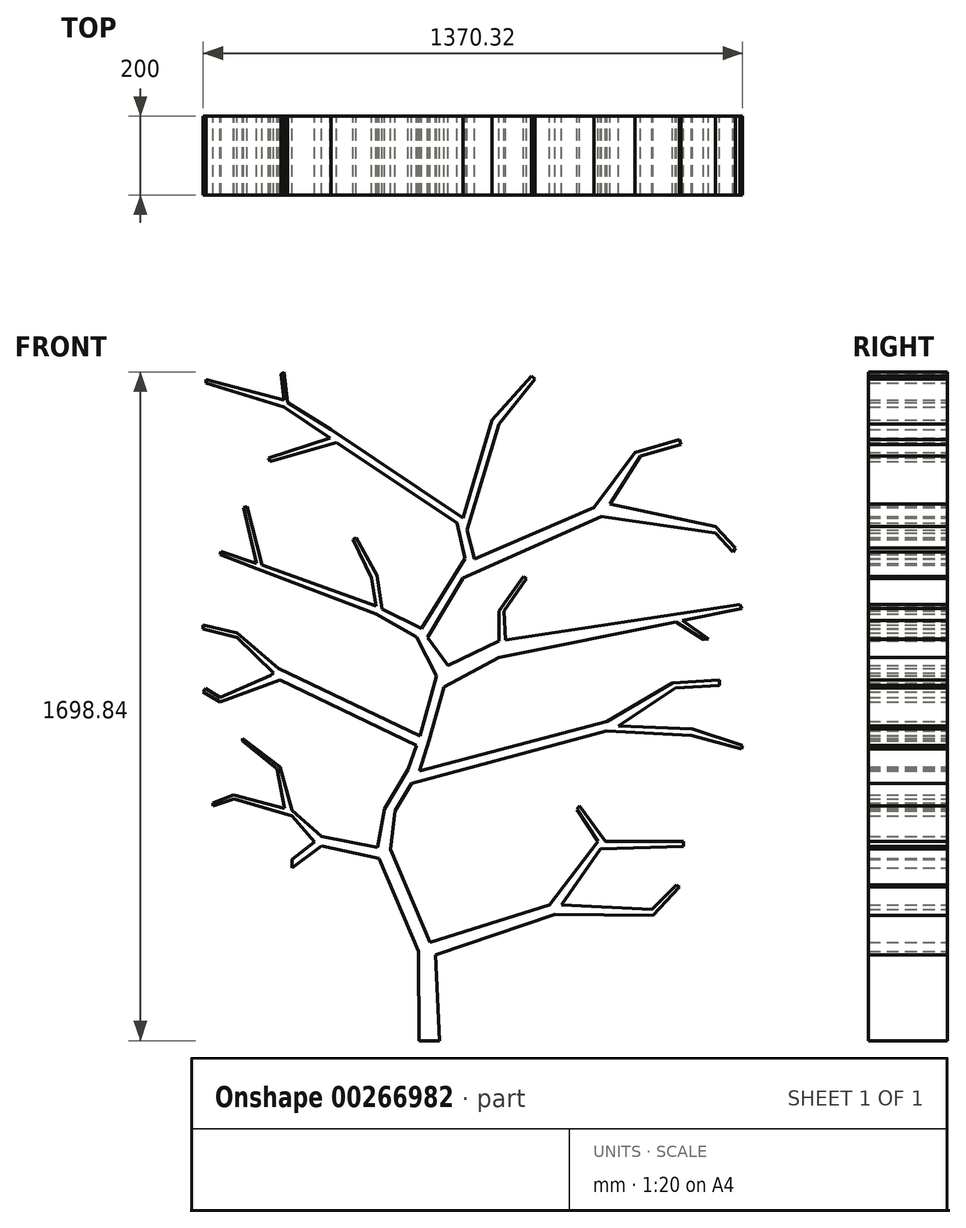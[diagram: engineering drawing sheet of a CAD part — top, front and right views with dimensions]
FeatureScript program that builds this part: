
annotation { "Feature Type Name" : "Feature", "Feature Type Description" : "" }
export const myFeature = defineFeature(function(context is Context, id is Id, definition is map)
    precondition{}
    {
        {
            var Q0;
            Q0=qCreatedBy(makeId("Front.planeOp"),FACE);
            var sketch = newSketch(context, id + "F0", { "sketchPlane" : qUnion([Q0])});
            skLineSegment(sketch, "E0", {"start": v(0, 0) * mm, "end": v(0, 750) * mm, "construction": true});
            skLineSegment(sketch, "E1", {"start": v(0, 750) * mm, "end": v(0, 0) * mm, "construction": true});
            skLineSegment(sketch, "E2", {"start": v(0, 0) * mm, "end": v(0, -750) * mm, "construction": true});
            skLineSegment(sketch, "E3", {"start": v(0, -750) * mm, "end": v(26, -750) * mm});
            skLineSegment(sketch, "E4", {"start": v(0, -750) * mm, "end": v(-26, -750) * mm});
            skLineSegment(sketch, "E5", {"start": v(0, -750) * mm, "end": v(0, -500) * mm, "construction": true});
            skLineSegment(sketch, "E6", {"start": v(-27.5, -522.62) * mm, "end": v(-26, -750) * mm});
            skLineSegment(sketch, "E7", {"start": v(-27.5, -522.62) * mm, "end": v(16.36, -532.36) * mm});
            skLineSegment(sketch, "E8", {"start": v(16.36, -532.36) * mm, "end": v(26, -750) * mm});
            skLineSegment(sketch, "E9", {"start": v(-86.68, -166.63) * mm, "end": v(-114.15, -161.22) * mm});
            skLineSegment(sketch, "E10", {"start": v(-98.77, -264.27) * mm, "end": v(16.36, -532.36) * mm});
            skLineSegment(sketch, "E11", {"start": v(-114.15, -161.22) * mm, "end": v(-131.21, -258.61) * mm});
            skLineSegment(sketch, "E12", {"start": v(-98.77, -264.27) * mm, "end": v(-86.68, -166.63) * mm});
            skLineSegment(sketch, "E13", {"start": v(-27.5, -522.62) * mm, "end": v(-137.38, -264.27) * mm});
            skPoint(sketch, "E14.endSnap0", {"position": v(-273.43, -243.18) * mm});
            skLineSegment(sketch, "E15", {"start": v(-348.87, -310.64) * mm, "end": v(-273.43, -255.18) * mm});
            skLineSegment(sketch, "E16", {"start": v(-348.87, -310.64) * mm, "end": v(-518.95, -310.64) * mm});
            skLineSegment(sketch, "E17", {"start": v(-518.95, -310.64) * mm, "end": v(-518.95, -300.64) * mm});
            skLineSegment(sketch, "E18", {"start": v(-518.95, -300.64) * mm, "end": v(-348.87, -289.78) * mm});
            skLineSegment(sketch, "E19", {"start": v(-273.43, -231.18) * mm, "end": v(-348.87, -164.52) * mm});
            skLineSegment(sketch, "E20", {"start": v(-348.87, -179.1) * mm, "end": v(-496.07, -135.48) * mm});
            skLineSegment(sketch, "E21", {"start": v(-496.07, -135.48) * mm, "end": v(-496.71, -125.5) * mm});
            skLineSegment(sketch, "E22", {"start": v(-496.71, -125.5) * mm, "end": v(-348.87, -164.52) * mm});
            skPoint(sketch, "E23.endSnap0", {"position": v(-422.79, -145.01) * mm});
            skLineSegment(sketch, "E24", {"start": v(-496.07, -135.48) * mm, "end": v(-548.63, -153.46) * mm});
            skLineSegment(sketch, "E25", {"start": v(-496.71, -125.5) * mm, "end": v(-548.63, -146.18) * mm});
            skLineSegment(sketch, "E26", {"start": v(-548.63, -146.18) * mm, "end": v(-548.63, -153.46) * mm});
            skLineSegment(sketch, "E27", {"start": v(-386.86, -60.16) * mm, "end": v(-367.22, -159.68) * mm});
            skLineSegment(sketch, "E28", {"start": v(-474.73, 18.31) * mm, "end": v(-474.73, 11.25) * mm});
            skLineSegment(sketch, "E29", {"start": v(-474.73, 11.25) * mm, "end": v(-386.86, -60.16) * mm});
            skLineSegment(sketch, "E30", {"start": v(-348.87, -179.1) * mm, "end": v(-348.87, -164.52) * mm});
            skLineSegment(sketch, "E31", {"start": v(-273.43, -231.18) * mm, "end": v(-131.21, -258.61) * mm});
            skLineSegment(sketch, "E32", {"start": v(-86.68, -166.63) * mm, "end": v(-24.85, -64.5) * mm});
            skLineSegment(sketch, "E33", {"start": v(-114.15, -161.22) * mm, "end": v(-53.7, -61.36) * mm});
            skLineSegment(sketch, "E34", {"start": v(-379.17, 166.4) * mm, "end": v(-531.36, 110.48) * mm});
            skLineSegment(sketch, "E35", {"start": v(-531.36, 110.48) * mm, "end": v(-551.07, 122.41) * mm});
            skLineSegment(sketch, "E36", {"start": v(-551.07, 122.41) * mm, "end": v(-573.98, 136.29) * mm});
            skLineSegment(sketch, "E37", {"start": v(-573.98, 136.29) * mm, "end": v(-568.07, 144.35) * mm});
            skLineSegment(sketch, "E38", {"start": v(-568.07, 144.35) * mm, "end": v(-531.83, 122.41) * mm});
            skLineSegment(sketch, "E39", {"start": v(-573.98, 295.89) * mm, "end": v(-573.98, 305.89) * mm});
            skLineSegment(sketch, "E40", {"start": v(-498.86, 342.03) * mm, "end": v(-507.68, 340.22) * mm});
            skLineSegment(sketch, "E41", {"start": v(-507.68, 340.22) * mm, "end": v(-498.86, 288.04) * mm});
            skLineSegment(sketch, "E42", {"start": v(-382.8, 195.37) * mm, "end": v(0, 13.26) * mm});
            skLineSegment(sketch, "E43", {"start": v(-488.64, 274.76) * mm, "end": v(-488.3, 285.3) * mm});
            skLineSegment(sketch, "E44", {"start": v(-488.64, 274.76) * mm, "end": v(-573.98, 295.89) * mm});
            skLineSegment(sketch, "E45", {"start": v(-498.86, 342.03) * mm, "end": v(-488.3, 285.3) * mm});
            skLineSegment(sketch, "E46", {"start": v(0, 13.26) * mm, "end": v(-24.85, -64.5) * mm});
            skLineSegment(sketch, "E47", {"start": v(-474.73, 18.31) * mm, "end": v(-379.07, -54.81) * mm});
            skLineSegment(sketch, "E48", {"start": v(-379.07, -54.81) * mm, "end": v(-348.87, -164.52) * mm});
            skLineSegment(sketch, "E49", {"start": v(-24.85, -64.5) * mm, "end": v(-53.7, -61.36) * mm});
            skLineSegment(sketch, "E50", {"start": v(18.3, 176.27) * mm, "end": v(-32.87, 275.32) * mm});
            skPoint(sketch, "E51.endSnap0", {"position": v(-435.55, 240.34) * mm});
            skLineSegment(sketch, "E52", {"start": v(-435.55, 448.7) * mm, "end": v(-531.1, 485.46) * mm});
            skLineSegment(sketch, "E53.1", {"start": v(47.7, 203.3) * mm, "end": v(-19.99, 296.75) * mm});
            skLineSegment(sketch, "E54", {"start": v(-463.33, 606.58) * mm, "end": v(-424.82, 458.12) * mm});
            skLineSegment(sketch, "E55", {"start": v(-531.1, 485.46) * mm, "end": v(-528.35, 492.64) * mm});
            skLineSegment(sketch, "E56", {"start": v(-528.35, 492.64) * mm, "end": v(-424.82, 458.12) * mm});
            skLineSegment(sketch, "E57", {"start": v(-435.55, 448.7) * mm, "end": v(-424.82, 458.12) * mm});
            skLineSegment(sketch, "E58", {"start": v(-463.33, 606.58) * mm, "end": v(-472.22, 605.16) * mm});
            skLineSegment(sketch, "E59", {"start": v(-186.22, 528.62) * mm, "end": v(-133.1, 431.59) * mm});
            skLineSegment(sketch, "E60", {"start": v(-193.05, 522.75) * mm, "end": v(-146.85, 425.73) * mm});
            skLineSegment(sketch, "E61", {"start": v(-146.85, 425.73) * mm, "end": v(-135.52, 354.13) * mm});
            skLineSegment(sketch, "E62", {"start": v(-193.05, 522.75) * mm, "end": v(-186.22, 528.62) * mm});
            skLineSegment(sketch, "E63", {"start": v(-19.99, 296.75) * mm, "end": v(90.32, 474.89) * mm});
            skLineSegment(sketch, "E64", {"start": v(90.32, 474.89) * mm, "end": v(69.97, 565) * mm});
            skLineSegment(sketch, "E65", {"start": v(-369.3, 860.1) * mm, "end": v(-567.2, 920.25) * mm});
            skLineSegment(sketch, "E66", {"start": v(-252.22, 781.46) * mm, "end": v(-407.64, 730.47) * mm});
            skLineSegment(sketch, "E67", {"start": v(-567.2, 920.25) * mm, "end": v(-567.2, 929.25) * mm});
            skLineSegment(sketch, "E68", {"start": v(-567.2, 929.25) * mm, "end": v(-369.3, 877.7) * mm});
            skLineSegment(sketch, "E69", {"start": v(-369.3, 877.7) * mm, "end": v(-248.8, 803.08) * mm});
            skLineSegment(sketch, "E70", {"start": v(115.18, 473.3) * mm, "end": v(-4.05, 274.75) * mm});
            skLineSegment(sketch, "E71", {"start": v(-248.8, 803.08) * mm, "end": v(-252.22, 781.46) * mm});
            skLineSegment(sketch, "E72", {"start": v(-407.64, 730.47) * mm, "end": v(-404.83, 721.92) * mm});
            skLineSegment(sketch, "E73", {"start": v(-404.83, 721.92) * mm, "end": v(-235, 769.9) * mm});
            skLineSegment(sketch, "E74", {"start": v(-369.3, 877.7) * mm, "end": v(-375.86, 943.95) * mm});
            skLineSegment(sketch, "E75", {"start": v(-375.86, 943.95) * mm, "end": v(-368.3, 948.84) * mm});
            skLineSegment(sketch, "E76", {"start": v(-368.3, 948.84) * mm, "end": v(-359.54, 871.65) * mm});
            skLineSegment(sketch, "E77", {"start": v(86.23, 578) * mm, "end": v(159.57, 827.14) * mm});
            skLineSegment(sketch, "E78", {"start": v(159.57, 827.14) * mm, "end": v(259.3, 938.6) * mm});
            skLineSegment(sketch, "E79", {"start": v(259.3, 938.6) * mm, "end": v(268.25, 930.6) * mm});
            skLineSegment(sketch, "E80", {"start": v(268.25, 930.6) * mm, "end": v(176.99, 817.27) * mm});
            skLineSegment(sketch, "E81", {"start": v(18.3, 176.27) * mm, "end": v(-23.78, 24.57) * mm});
            skLineSegment(sketch, "E82", {"start": v(115.18, 473.3) * mm, "end": v(96.35, 547.3) * mm});
            skLineSegment(sketch, "E83", {"start": v(-248.8, 803.08) * mm, "end": v(102.3, 567.22) * mm});
            skLineSegment(sketch, "E84", {"start": v(96.35, 547.3) * mm, "end": v(102.3, 567.22) * mm});
            skLineSegment(sketch, "E85", {"start": v(176.99, 817.27) * mm, "end": v(102.3, 567.22) * mm});
            skLineSegment(sketch, "E86", {"start": v(-252.22, 781.46) * mm, "end": v(96.35, 547.3) * mm});
            skLineSegment(sketch, "E87", {"start": v(-369.3, 860.1) * mm, "end": v(-252.22, 781.46) * mm});
            skLineSegment(sketch, "E88", {"start": v(-369.3, 860.1) * mm, "end": v(-369.3, 877.7) * mm});
            skLineSegment(sketch, "E89", {"start": v(-435.55, 448.7) * mm, "end": v(-135.52, 333.76) * mm});
            skLineSegment(sketch, "E90", {"start": v(-135.52, 333.76) * mm, "end": v(-32.87, 275.32) * mm});
            skLineSegment(sketch, "E91", {"start": v(-135.52, 354.13) * mm, "end": v(-19.99, 296.75) * mm});
            skLineSegment(sketch, "E92", {"start": v(-133.1, 431.59) * mm, "end": v(-119.96, 346.4) * mm});
            skLineSegment(sketch, "E93", {"start": v(-424.82, 458.12) * mm, "end": v(-135.52, 354.13) * mm});
            skLineSegment(sketch, "E94", {"start": v(-135.52, 333.76) * mm, "end": v(-135.52, 354.13) * mm});
            skLineSegment(sketch, "E95", {"start": v(115.18, 473.3) * mm, "end": v(418.92, 604.57) * mm});
            skLineSegment(sketch, "E96", {"start": v(437.9, 581.4) * mm, "end": v(86.38, 425.35) * mm});
            skLineSegment(sketch, "E97", {"start": v(418.92, 604.57) * mm, "end": v(437.9, 581.4) * mm});
            skLineSegment(sketch, "E98", {"start": v(536.94, 735.86) * mm, "end": v(639.59, 765.23) * mm});
            skLineSegment(sketch, "E99", {"start": v(639.59, 765.23) * mm, "end": v(636.29, 776.77) * mm});
            skLineSegment(sketch, "E100", {"start": v(636.29, 776.77) * mm, "end": v(522.92, 744.33) * mm});
            skLineSegment(sketch, "E101", {"start": v(536.94, 735.86) * mm, "end": v(522.92, 744.33) * mm});
            skLineSegment(sketch, "E102", {"start": v(536.94, 735.86) * mm, "end": v(437.9, 581.4) * mm});
            skLineSegment(sketch, "E103", {"start": v(522.92, 744.33) * mm, "end": v(418.92, 604.57) * mm});
            skLineSegment(sketch, "E104", {"start": v(458.65, 613.76) * mm, "end": v(726.6, 556.88) * mm});
            skLineSegment(sketch, "E105", {"start": v(726.6, 556.88) * mm, "end": v(726.6, 539.26) * mm});
            skLineSegment(sketch, "E106", {"start": v(726.6, 539.26) * mm, "end": v(437.9, 581.4) * mm});
            skLineSegment(sketch, "E107", {"start": v(726.6, 539.26) * mm, "end": v(771.62, 491.3) * mm});
            skLineSegment(sketch, "E108", {"start": v(771.62, 491.3) * mm, "end": v(778.1, 501.4) * mm});
            skLineSegment(sketch, "E109", {"start": v(778.1, 501.4) * mm, "end": v(726.6, 556.88) * mm});
            skLineSegment(sketch, "E110", {"start": v(47.7, 203.3) * mm, "end": v(177.76, 265.35) * mm});
            skLineSegment(sketch, "E111", {"start": v(177.76, 265.35) * mm, "end": v(789.64, 358.7) * mm});
            skLineSegment(sketch, "E112", {"start": v(789.64, 358.7) * mm, "end": v(794.81, 347.86) * mm});
            skLineSegment(sketch, "E113", {"start": v(794.81, 347.86) * mm, "end": v(177.76, 223.87) * mm});
            skLineSegment(sketch, "E114", {"start": v(177.76, 223.87) * mm, "end": v(177.76, 265.35) * mm});
            skLineSegment(sketch, "E115", {"start": v(177.76, 265.35) * mm, "end": v(177.76, 342.1) * mm});
            skLineSegment(sketch, "E116", {"start": v(177.76, 342.1) * mm, "end": v(239.99, 429.21) * mm});
            skLineSegment(sketch, "E117", {"start": v(239.99, 429.21) * mm, "end": v(247.31, 423.98) * mm});
            skLineSegment(sketch, "E118", {"start": v(177.76, 342.1) * mm, "end": v(189.76, 342.1) * mm});
            skLineSegment(sketch, "E119", {"start": v(189.76, 342.1) * mm, "end": v(247.31, 423.98) * mm});
            skLineSegment(sketch, "E120", {"start": v(189.76, 342.1) * mm, "end": v(193.3, 267.72) * mm});
            skLineSegment(sketch, "E121", {"start": v(626.5, 314.04) * mm, "end": v(696.97, 268.78) * mm});
            skLineSegment(sketch, "E122", {"start": v(696.97, 268.78) * mm, "end": v(708.74, 271.15) * mm});
            skLineSegment(sketch, "E123", {"start": v(708.74, 271.15) * mm, "end": v(643.63, 317.48) * mm});
            skLineSegment(sketch, "E124", {"start": v(177.76, 223.87) * mm, "end": v(6.3, 133) * mm});
            skLineSegment(sketch, "E125", {"start": v(0, 13.26) * mm, "end": v(36.96, 149.25) * mm});
            skLineSegment(sketch, "E126", {"start": v(36.96, 149.25) * mm, "end": v(47.7, 203.3) * mm});
            skPoint(sketch, "E127", {"position": v(42.33, 176.27) * mm});
            skLineSegment(sketch, "E128", {"start": v(-24.85, -64.5) * mm, "end": v(451.57, 61.3) * mm});
            skLineSegment(sketch, "E129", {"start": v(451.57, 61.3) * mm, "end": v(618.03, 159.08) * mm});
            skLineSegment(sketch, "E130", {"start": v(618.03, 159.08) * mm, "end": v(625.63, 146.15) * mm});
            skLineSegment(sketch, "E131", {"start": v(625.63, 146.15) * mm, "end": v(467.87, 41.5) * mm});
            skLineSegment(sketch, "E132", {"start": v(467.87, 41.5) * mm, "end": v(-44.48, -96.93) * mm});
            skLineSegment(sketch, "E133", {"start": v(467.87, 41.5) * mm, "end": v(451.57, 61.3) * mm});
            skLineSegment(sketch, "E134", {"start": v(618.03, 159.08) * mm, "end": v(737, 166.41) * mm});
            skLineSegment(sketch, "E135", {"start": v(737, 166.41) * mm, "end": v(737.85, 152.49) * mm});
            skLineSegment(sketch, "E136", {"start": v(737.85, 152.49) * mm, "end": v(625.63, 146.15) * mm});
            skLineSegment(sketch, "E137", {"start": v(669.02, 41.5) * mm, "end": v(796.34, 0) * mm});
            skLineSegment(sketch, "E138", {"start": v(796.34, 0) * mm, "end": v(793.55, -8.56) * mm});
            skLineSegment(sketch, "E139", {"start": v(793.55, -8.56) * mm, "end": v(666.44, 25.38) * mm});
            skLineSegment(sketch, "E140", {"start": v(480.75, 50.05) * mm, "end": v(669.02, 41.5) * mm});
            skLineSegment(sketch, "E141", {"start": v(666.44, 25.38) * mm, "end": v(450.42, 36.8) * mm});
            skLineSegment(sketch, "E142", {"start": v(2.57, -500.24) * mm, "end": v(305.08, -405.5) * mm});
            skLineSegment(sketch, "E143", {"start": v(305.08, -405.5) * mm, "end": v(428.39, -243.98) * mm});
            skLineSegment(sketch, "E144", {"start": v(428.39, -243.98) * mm, "end": v(646.4, -243.98) * mm});
            skLineSegment(sketch, "E145", {"start": v(448.05, -243.98) * mm, "end": v(382.33, -153.22) * mm});
            skLineSegment(sketch, "E146", {"start": v(335.48, -405.5) * mm, "end": v(565.52, -415.99) * mm});
            skLineSegment(sketch, "E147", {"start": v(565.52, -415.99) * mm, "end": v(628.16, -354.32) * mm});
            skLineSegment(sketch, "E148", {"start": v(628.16, -354.32) * mm, "end": v(635.32, -359.78) * mm});
            skLineSegment(sketch, "E149", {"start": v(635.32, -359.78) * mm, "end": v(568.45, -431.65) * mm});
            skLineSegment(sketch, "E150", {"start": v(382.33, -153.22) * mm, "end": v(375.05, -162.76) * mm});
            skLineSegment(sketch, "E151", {"start": v(375.05, -162.76) * mm, "end": v(428.39, -243.98) * mm});
            skLineSegment(sketch, "E152", {"start": v(646.4, -243.98) * mm, "end": v(646.4, -255.98) * mm});
            skLineSegment(sketch, "E153", {"start": v(646.4, -255.98) * mm, "end": v(434.8, -262.99) * mm});
            skLineSegment(sketch, "E154", {"start": v(565.52, -415.99) * mm, "end": v(568.45, -431.65) * mm});
            skLineSegment(sketch, "E155", {"start": v(16.36, -532.36) * mm, "end": v(319.28, -428.74) * mm});
            skLineSegment(sketch, "E156", {"start": v(319.28, -428.74) * mm, "end": v(305.08, -405.5) * mm});
            skLineSegment(sketch, "E157", {"start": v(319.28, -428.74) * mm, "end": v(568.45, -431.65) * mm});
            skLineSegment(sketch, "E158", {"start": v(-131.21, -258.61) * mm, "end": v(-98.84, -264.86) * mm});
            skLineSegment(sketch, "E159", {"start": v(-137.38, -264.27) * mm, "end": v(-140.55, -256.8) * mm});
            skLineSegment(sketch, "E160", {"start": v(-98.5, -264.92) * mm, "end": v(-98.77, -264.27) * mm});
            skLineSegment(sketch, "E161", {"start": v(-98.5, -264.92) * mm, "end": v(-140.55, -256.8) * mm});
            skLineSegment(sketch, "E162", {"start": v(-273.43, -255.18) * mm, "end": v(-127.67, -287.11) * mm});
            skLineSegment(sketch, "E163", {"start": v(-273.43, -231.18) * mm, "end": v(-273.43, -255.18) * mm});
            skLineSegment(sketch, "E164", {"start": v(-348.87, -289.78) * mm, "end": v(-273.43, -231.18) * mm});
            skLineSegment(sketch, "E165", {"start": v(-348.87, -179.1) * mm, "end": v(-291.16, -244.94) * mm});
            skLineSegment(sketch, "E166", {"start": v(-386.86, -60.16) * mm, "end": v(-379.07, -54.81) * mm});
            skLineSegment(sketch, "E167", {"start": v(-23.78, 24.57) * mm, "end": v(-53.7, -61.36) * mm});
            skLineSegment(sketch, "E168", {"start": v(-379.17, 166.4) * mm, "end": v(-32.12, 0.63) * mm});
            skLineSegment(sketch, "E169", {"start": v(-531.83, 122.41) * mm, "end": v(-531.36, 110.48) * mm});
            skLineSegment(sketch, "E170", {"start": v(-382.8, 195.37) * mm, "end": v(-402.95, 177.76) * mm});
            skLineSegment(sketch, "E171", {"start": v(-379.17, 166.4) * mm, "end": v(-402.95, 177.76) * mm});
            skLineSegment(sketch, "E172", {"start": v(-402.95, 177.76) * mm, "end": v(-531.83, 122.41) * mm});
            skLineSegment(sketch, "E173", {"start": v(-488.64, 274.76) * mm, "end": v(-395.14, 184.59) * mm});
            skLineSegment(sketch, "E174", {"start": v(-488.35, 285.55) * mm, "end": v(-382.8, 195.37) * mm});
            skLineSegment(sketch, "E175", {"start": v(-573.98, 305.89) * mm, "end": v(-488.3, 285.3) * mm});
            skLineSegment(sketch, "E176", {"start": v(18.3, 176.27) * mm, "end": v(47.7, 203.3) * mm});
            skLineSegment(sketch, "E177", {"start": v(-32.87, 275.32) * mm, "end": v(-19.99, 296.75) * mm});
            skLineSegment(sketch, "E178", {"start": v(-472.22, 605.16) * mm, "end": v(-439.23, 462.93) * mm});
            skLineSegment(sketch, "E179", {"start": v(115.18, 473.3) * mm, "end": v(90.32, 474.89) * mm});
            skLineSegment(sketch, "E180", {"start": v(159.57, 827.14) * mm, "end": v(176.99, 817.27) * mm});
            skLineSegment(sketch, "E181", {"start": v(319.28, -428.74) * mm, "end": v(448.05, -243.98) * mm});
            skLineSegment(sketch, "E182", {"start": v(-348.87, -310.64) * mm, "end": v(-348.87, -289.78) * mm});
            skSolve(sketch);
        }
        {
            var Q0;
            {var subQ0=sQuery(id+"F0.wireOp",EDGE,"E71");Q0=makeQuery(id+"F0.imprint","IMPRINT",FACE,{"disambiguationData":[TD([[makeQuery(id+"F0.imprint","IMPRINT",EDGE,{"derivedFrom":subQ0}),-1.0]])]});}
            var Q1;
            {var subQ0=sQuery(id+"F0.wireOp",EDGE,"E77");Q1=makeQuery(id+"F0.imprint","IMPRINT",FACE,{"disambiguationData":[TD([[makeQuery(id+"F0.imprint","IMPRINT",EDGE,{"derivedFrom":subQ0}),-1.0]])]});}
            var Q2;
            Q2=makeQuery(id+"F0.imprint","IMPRINT",FACE,{"disambiguationData":[TD([[makeQuery(id+"F0.imprint","IMPRINT",EDGE,{"derivedFrom":sQuery(id+"F0.wireOp",EDGE,"E110")}),-1.0]])]});
            var Q3;
            {var subQ2=sQuery(id+"F0.wireOp",EDGE,"E43");Q3=makeQuery(id+"F0.imprint","IMPRINT",FACE,{"disambiguationData":[TD([[makeQuery(id+"F0.imprint","IMPRINT",EDGE,{"derivedFrom":subQ2}),-1.0]])]});}
            var Q4;
            Q4=makeQuery(id+"F0.imprint","IMPRINT",FACE,{"disambiguationData":[TD([[makeQuery(id+"F0.imprint","IMPRINT",EDGE,{"derivedFrom":sQuery(id+"F0.wireOp",EDGE,"E34")}),-1.0]])]});
            var Q5;
            {var subQ2=sQuery(id+"F0.wireOp",EDGE,"E142");Q5=makeQuery(id+"F0.imprint","IMPRINT",FACE,{"disambiguationData":[TD([[makeQuery(id+"F0.imprint","IMPRINT",EDGE,{"derivedFrom":subQ2}),-1.0]])]});}
            var Q6;
            {var subQ5=sQuery(id+"F0.wireOp",EDGE,"E63");Q6=makeQuery(id+"F0.imprint","IMPRINT",FACE,{"disambiguationData":[TD([[makeQuery(id+"F0.imprint","IMPRINT",EDGE,{"derivedFrom":subQ5}),-1.0]])]});}
            var Q7;
            {var subQ1=sQuery(id+"F0.wireOp",EDGE,"E7");Q7=makeQuery(id+"F0.imprint","IMPRINT",FACE,{"disambiguationData":[TD([[makeQuery(id+"F0.imprint","IMPRINT",EDGE,{"derivedFrom":subQ1}),1.0]])]});}
            var Q8;
            {var subQ5=sQuery(id+"F0.wireOp",EDGE,"E128");Q8=makeQuery(id+"F0.imprint","IMPRINT",FACE,{"disambiguationData":[TD([[makeQuery(id+"F0.imprint","IMPRINT",EDGE,{"derivedFrom":subQ5}),-1.0]])]});}
            var Q9;
            Q9=makeQuery(id+"F0.imprint","IMPRINT",FACE,{"disambiguationData":[TD([[makeQuery(id+"F0.imprint","IMPRINT",EDGE,{"derivedFrom":sQuery(id+"F0.wireOp",EDGE,"E15")}),1.0]])]});
            var Q10;
            {var subQ5=sQuery(id+"F0.wireOp",EDGE,"E168");Q10=makeQuery(id+"F0.imprint","IMPRINT",FACE,{"disambiguationData":[TD([[makeQuery(id+"F0.imprint","IMPRINT",EDGE,{"derivedFrom":subQ5}),1.0]])]});}
            var Q11;
            {var subQ0=sQuery(id+"F0.wireOp",EDGE,"E54");Q11=makeQuery(id+"F0.imprint","IMPRINT",FACE,{"disambiguationData":[TD([[makeQuery(id+"F0.imprint","IMPRINT",EDGE,{"derivedFrom":subQ0}),-1.0]])]});}
            var Q12;
            {var subQ0=sQuery(id+"F0.wireOp",EDGE,"E95");Q12=makeQuery(id+"F0.imprint","IMPRINT",FACE,{"disambiguationData":[TD([[makeQuery(id+"F0.imprint","IMPRINT",EDGE,{"derivedFrom":subQ0}),-1.0]])]});}
            var Q13;
            {var subQ0=sQuery(id+"F0.wireOp",EDGE,"E66");Q13=makeQuery(id+"F0.imprint","IMPRINT",FACE,{"disambiguationData":[TD([[makeQuery(id+"F0.imprint","IMPRINT",EDGE,{"derivedFrom":subQ0}),1.0]])]});}
            var Q14;
            Q14=makeQuery(id+"F0.imprint","IMPRINT",FACE,{"disambiguationData":[TD([[makeQuery(id+"F0.imprint","IMPRINT",EDGE,{"derivedFrom":sQuery(id+"F0.wireOp",EDGE,"E59")}),-1.0]])]});
            var Q15;
            {var subQ2=sQuery(id+"F0.wireOp",EDGE,"E104");Q15=makeQuery(id+"F0.imprint","IMPRINT",FACE,{"disambiguationData":[TD([[makeQuery(id+"F0.imprint","IMPRINT",EDGE,{"derivedFrom":subQ2}),-1.0]])]});}
            var Q16;
            Q16=makeQuery(id+"F0.imprint","IMPRINT",FACE,{"disambiguationData":[TD([[makeQuery(id+"F0.imprint","IMPRINT",EDGE,{"derivedFrom":sQuery(id+"F0.wireOp",EDGE,"E98")}),1.0]])]});
            var Q17;
            Q17=makeQuery(id+"F0.imprint","IMPRINT",FACE,{"disambiguationData":[TD([[makeQuery(id+"F0.imprint","IMPRINT",EDGE,{"derivedFrom":sQuery(id+"F0.wireOp",EDGE,"E137")}),-1.0]])]});
            var Q18;
            Q18=makeQuery(id+"F0.imprint","IMPRINT",FACE,{"disambiguationData":[TD([[makeQuery(id+"F0.imprint","IMPRINT",EDGE,{"derivedFrom":sQuery(id+"F0.wireOp",EDGE,"E146")}),-1.0]])]});
            var Q19;
            {var subQ0=sQuery(id+"F0.wireOp",EDGE,"E125");Q19=makeQuery(id+"F0.imprint","IMPRINT",FACE,{"disambiguationData":[TD([[makeQuery(id+"F0.imprint","IMPRINT",EDGE,{"derivedFrom":subQ0}),1.0]])]});}
            var Q20;
            {var subQ1=sQuery(id+"F0.wireOp",EDGE,"E112");Q20=makeQuery(id+"F0.imprint","IMPRINT",FACE,{"disambiguationData":[TD([[makeQuery(id+"F0.imprint","IMPRINT",EDGE,{"derivedFrom":subQ1}),-1.0]])]});}
            var Q21;
            Q21=makeQuery(id+"F0.imprint","IMPRINT",FACE,{"disambiguationData":[TD([[makeQuery(id+"F0.imprint","IMPRINT",EDGE,{"derivedFrom":sQuery(id+"F0.wireOp",EDGE,"E57")}),-1.0]])]});
            var Q22;
            Q22=makeQuery(id+"F0.imprint","IMPRINT",FACE,{"disambiguationData":[TD([[makeQuery(id+"F0.imprint","IMPRINT",EDGE,{"derivedFrom":sQuery(id+"F0.wireOp",EDGE,"E78")}),-1.0]])]});
            var Q23;
            {var subQ0=sQuery(id+"F0.wireOp",EDGE,"E19");Q23=makeQuery(id+"F0.imprint","IMPRINT",FACE,{"disambiguationData":[TD([[makeQuery(id+"F0.imprint","IMPRINT",EDGE,{"derivedFrom":subQ0}),1.0]])]});}
            var Q24;
            {var subQ3=sQuery(id+"F0.wireOp",EDGE,"E9");Q24=makeQuery(id+"F0.imprint","IMPRINT",FACE,{"disambiguationData":[TD([[makeQuery(id+"F0.imprint","IMPRINT",EDGE,{"derivedFrom":subQ3}),-1.0]])]});}
            var Q25;
            {var subQ1=sQuery(id+"F0.wireOp",EDGE,"E97");Q25=makeQuery(id+"F0.imprint","IMPRINT",FACE,{"disambiguationData":[TD([[makeQuery(id+"F0.imprint","IMPRINT",EDGE,{"derivedFrom":subQ1}),1.0]])]});}
            var Q26;
            {var subQ2=sQuery(id+"F0.wireOp",EDGE,"E27");Q26=makeQuery(id+"F0.imprint","IMPRINT",FACE,{"disambiguationData":[TD([[makeQuery(id+"F0.imprint","IMPRINT",EDGE,{"derivedFrom":subQ2}),1.0]])]});}
            var Q27;
            Q27=makeQuery(id+"F0.imprint","IMPRINT",FACE,{"disambiguationData":[TD([[makeQuery(id+"F0.imprint","IMPRINT",EDGE,{"derivedFrom":sQuery(id+"F0.wireOp",EDGE,"E90")}),1.0]])]});
            var Q28;
            Q28=makeQuery(id+"F0.imprint","IMPRINT",FACE,{"disambiguationData":[TD([[makeQuery(id+"F0.imprint","IMPRINT",EDGE,{"derivedFrom":sQuery(id+"F0.wireOp",EDGE,"E9")}),1.0]])]});
            var Q29;
            Q29=makeQuery(id+"F0.imprint","IMPRINT",FACE,{"disambiguationData":[TD([[makeQuery(id+"F0.imprint","IMPRINT",EDGE,{"derivedFrom":sQuery(id+"F0.wireOp",EDGE,"E31")}),-1.0]])]});
            var Q30;
            Q30=makeQuery(id+"F0.imprint","IMPRINT",FACE,{"disambiguationData":[TD([[makeQuery(id+"F0.imprint","IMPRINT",EDGE,{"derivedFrom":sQuery(id+"F0.wireOp",EDGE,"E130")}),1.0]])]});
            var Q31;
            {var subQ5=sQuery(id+"F0.wireOp",EDGE,"E143");Q31=makeQuery(id+"F0.imprint","IMPRINT",FACE,{"disambiguationData":[TD([[makeQuery(id+"F0.imprint","IMPRINT",EDGE,{"derivedFrom":subQ5}),-1.0]])]});}
            var Q32;
            Q32=makeQuery(id+"F0.imprint","IMPRINT",FACE,{"disambiguationData":[TD([[makeQuery(id+"F0.imprint","IMPRINT",EDGE,{"derivedFrom":sQuery(id+"F0.wireOp",EDGE,"E50")}),-1.0]])]});
            var Q33;
            {var subQ2=sQuery(id+"F0.wireOp",EDGE,"E145");Q33=makeQuery(id+"F0.imprint","IMPRINT",FACE,{"disambiguationData":[TD([[makeQuery(id+"F0.imprint","IMPRINT",EDGE,{"derivedFrom":subQ2}),1.0]])]});}
            var Q34;
            Q34=makeQuery(id+"F0.imprint","IMPRINT",FACE,{"disambiguationData":[TD([[makeQuery(id+"F0.imprint","IMPRINT",EDGE,{"derivedFrom":sQuery(id+"F0.wireOp",EDGE,"E129")}),-1.0]])]});
            var Q35;
            Q35=makeQuery(id+"F0.imprint","IMPRINT",FACE,{"disambiguationData":[TD([[makeQuery(id+"F0.imprint","IMPRINT",EDGE,{"derivedFrom":sQuery(id+"F0.wireOp",EDGE,"E65")}),-1.0]])]});
            var Q36;
            {var subQ3=sQuery(id+"F0.wireOp",EDGE,"E71");Q36=makeQuery(id+"F0.imprint","IMPRINT",FACE,{"disambiguationData":[TD([[makeQuery(id+"F0.imprint","IMPRINT",EDGE,{"derivedFrom":subQ3}),1.0]])]});}
            var Q37;
            {var subQ0=sQuery(id+"F0.wireOp",EDGE,"E64");Q37=makeQuery(id+"F0.imprint","IMPRINT",FACE,{"disambiguationData":[TD([[makeQuery(id+"F0.imprint","IMPRINT",EDGE,{"derivedFrom":subQ0}),-1.0]])]});}
            var Q38;
            Q38=makeQuery(id+"F0.imprint","IMPRINT",FACE,{"disambiguationData":[TD([[makeQuery(id+"F0.imprint","IMPRINT",EDGE,{"derivedFrom":sQuery(id+"F0.wireOp",EDGE,"E3")}),1.0]])]});
            var Q39;
            {var subQ0=sQuery(id+"F0.wireOp",EDGE,"E115");Q39=makeQuery(id+"F0.imprint","IMPRINT",FACE,{"disambiguationData":[TD([[makeQuery(id+"F0.imprint","IMPRINT",EDGE,{"derivedFrom":subQ0}),-1.0]])]});}
            var Q40;
            Q40=makeQuery(id+"F0.imprint","IMPRINT",FACE,{"disambiguationData":[TD([[makeQuery(id+"F0.imprint","IMPRINT",EDGE,{"derivedFrom":sQuery(id+"F0.wireOp",EDGE,"E21")}),1.0]])]});
            var Q41;
            Q41=makeQuery(id+"F0.imprint","IMPRINT",FACE,{"disambiguationData":[TD([[makeQuery(id+"F0.imprint","IMPRINT",EDGE,{"derivedFrom":sQuery(id+"F0.wireOp",EDGE,"E105")}),1.0]])]});
            var Q42;
            Q42=makeQuery(id+"F0.imprint","IMPRINT",FACE,{"disambiguationData":[TD([[makeQuery(id+"F0.imprint","IMPRINT",EDGE,{"derivedFrom":sQuery(id+"F0.wireOp",EDGE,"E20")}),-1.0]])]});
            var Q43;
            Q43=makeQuery(id+"F0.imprint","IMPRINT",FACE,{"disambiguationData":[TD([[makeQuery(id+"F0.imprint","IMPRINT",EDGE,{"derivedFrom":sQuery(id+"F0.wireOp",EDGE,"E147")}),-1.0]])]});
            var Q44;
            {var subQ0=sQuery(id+"F0.wireOp",EDGE,"E74");Q44=makeQuery(id+"F0.imprint","IMPRINT",FACE,{"disambiguationData":[TD([[makeQuery(id+"F0.imprint","IMPRINT",EDGE,{"derivedFrom":subQ0}),-1.0]])]});}
            var Q45;
            Q45=makeQuery(id+"F0.imprint","IMPRINT",FACE,{"disambiguationData":[TD([[makeQuery(id+"F0.imprint","IMPRINT",EDGE,{"derivedFrom":sQuery(id+"F0.wireOp",EDGE,"E52")}),-1.0]])]});
            var Q46;
            Q46=makeQuery(id+"F0.imprint","IMPRINT",FACE,{"disambiguationData":[TD([[makeQuery(id+"F0.imprint","IMPRINT",EDGE,{"derivedFrom":sQuery(id+"F0.wireOp",EDGE,"E39")}),-1.0]])]});
            var Q47;
            {var subQ4=sQuery(id+"F0.wireOp",EDGE,"E126");Q47=makeQuery(id+"F0.imprint","IMPRINT",FACE,{"disambiguationData":[TD([[makeQuery(id+"F0.imprint","IMPRINT",EDGE,{"derivedFrom":subQ4}),1.0]])]});}
            var Q48;
            Q48=makeQuery(id+"F0.imprint","IMPRINT",FACE,{"disambiguationData":[TD([[makeQuery(id+"F0.imprint","IMPRINT",EDGE,{"derivedFrom":sQuery(id+"F0.wireOp",EDGE,"E116")}),-1.0]])]});
            var Q49;
            Q49=makeQuery(id+"F0.imprint","IMPRINT",FACE,{"disambiguationData":[TD([[makeQuery(id+"F0.imprint","IMPRINT",EDGE,{"derivedFrom":sQuery(id+"F0.wireOp",EDGE,"E28")}),1.0]])]});
            var Q50;
            {var subQ0=sQuery(id+"F0.wireOp",EDGE,"E121");Q50=makeQuery(id+"F0.imprint","IMPRINT",FACE,{"disambiguationData":[TD([[makeQuery(id+"F0.imprint","IMPRINT",EDGE,{"derivedFrom":subQ0}),1.0]])]});}
            var Q51;
            {var subQ5=sQuery(id+"F0.wireOp",EDGE,"E46");Q51=makeQuery(id+"F0.imprint","IMPRINT",FACE,{"disambiguationData":[TD([[makeQuery(id+"F0.imprint","IMPRINT",EDGE,{"derivedFrom":subQ5}),-1.0]])]});}
            var Q52;
            {var subQ0=sQuery(id+"F0.wireOp",EDGE,"E152");Q52=makeQuery(id+"F0.imprint","IMPRINT",FACE,{"disambiguationData":[TD([[makeQuery(id+"F0.imprint","IMPRINT",EDGE,{"derivedFrom":subQ0}),-1.0]])]});}
            var Q53;
            Q53=makeQuery(id+"F0.imprint","IMPRINT",FACE,{"disambiguationData":[TD([[makeQuery(id+"F0.imprint","IMPRINT",EDGE,{"derivedFrom":sQuery(id+"F0.wireOp",EDGE,"E35")}),-1.0]])]});
            extrude(context, id + "F1", {"entities" : qUnion([Q0, Q1, Q2, Q3, Q4, Q5, Q6, Q7, Q8, Q9, Q10, Q11, Q12, Q13, Q14, Q15, Q16, Q17, Q18, Q19, Q20, Q21, Q22, Q23, Q24, Q25, Q26, Q27, Q28, Q29, Q30, Q31, Q32, Q33, Q34, Q35, Q36, Q37, Q38, Q39, Q40, Q41, Q42, Q43, Q44, Q45, Q46, Q47, Q48, Q49, Q50, Q51, Q52, Q53]), "depth" : 200 * mm});
        }
    });
